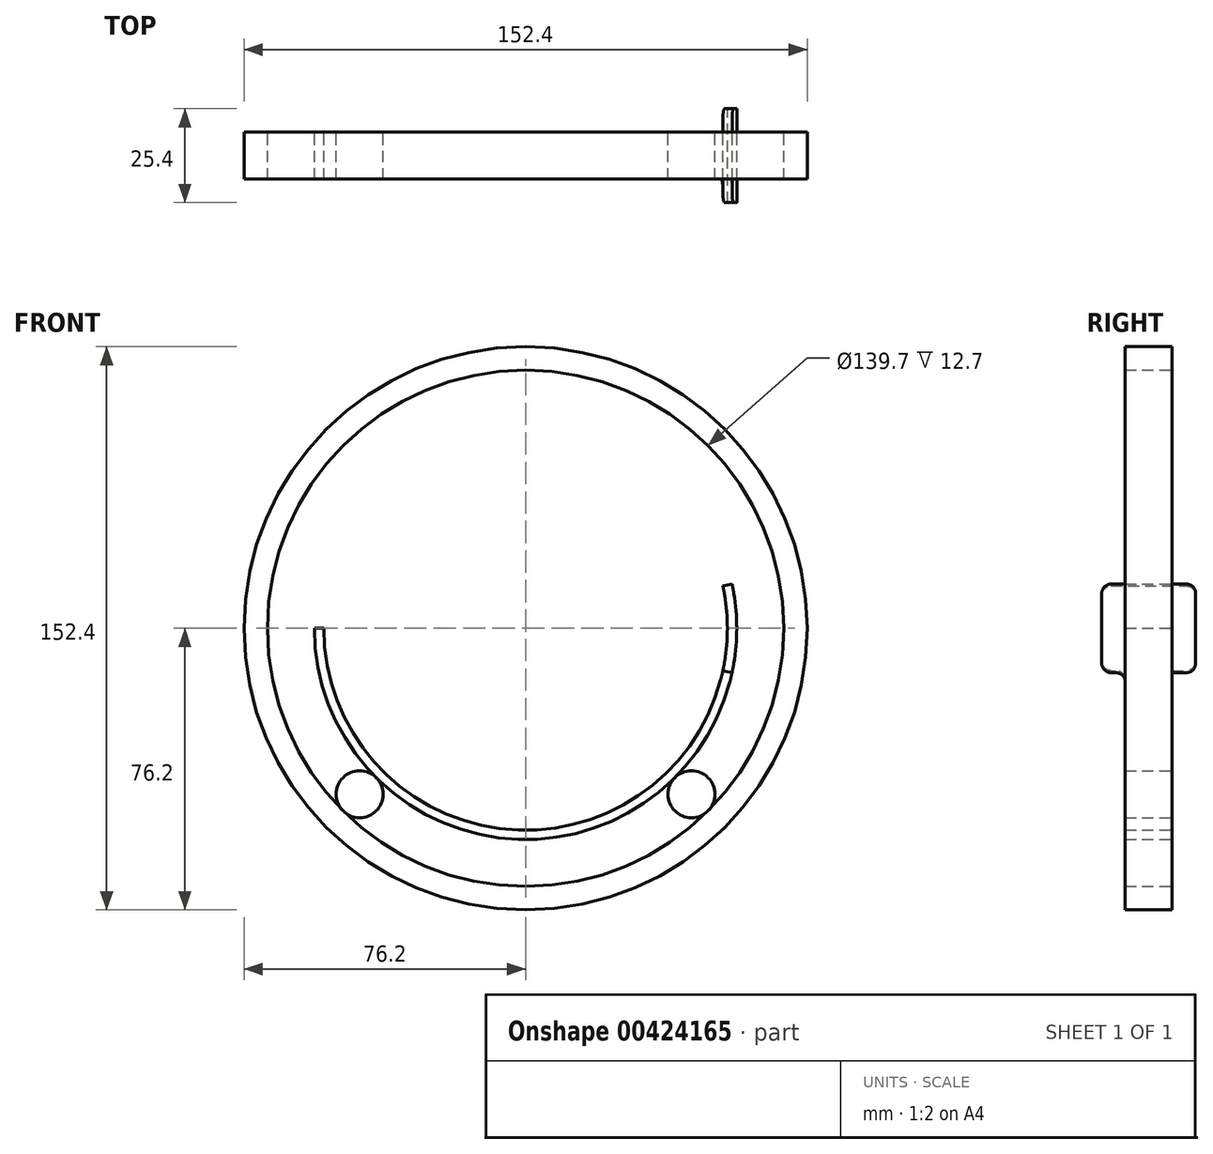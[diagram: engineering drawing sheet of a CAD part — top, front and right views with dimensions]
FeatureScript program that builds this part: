
annotation { "Feature Type Name" : "Feature", "Feature Type Description" : "" }
export const myFeature = defineFeature(function(context is Context, id is Id, definition is map)
    precondition{}
    {
        {
            assignVariable(context, id + "F0", {"name" : "SgAngle", "anyValue" : 45 * degree});
        }
        {
            var Q0;
            Q0=qCreatedBy(makeId("Front.planeOp"),FACE);
            var sketch = newSketch(context, id + "F1", { "sketchPlane" : qUnion([Q0])});
            skCircle(sketch, "E0", {"center": v(0, 0) * mm, "radius": 76.2 * mm});
            skCircle(sketch, "E1", {"center": v(0, 0) * mm, "radius": 69.85 * mm});
            skCircle(sketch, "E2", {"center": v(-44.9, -44.9) * mm, "radius": 6.35 * mm});
            skLineSegment(sketch, "E3", {"start": v(0, 0) * mm, "end": v(0, -76.2) * mm, "construction": true});
            skLineSegment(sketch, "E4", {"start": v(0, -76.2) * mm, "end": v(-76.2, -76.2) * mm, "construction": true});
            skLineSegment(sketch, "E5", {"start": v(-76.2, -76.2) * mm, "end": v(0, 0) * mm, "construction": true});
            skSolve(sketch);
        }
        {
            var Q0;
            Q0=makeQuery(id+"F1.imprint","IMPRINT",FACE,{"disambiguationData":[TD([[makeQuery(id+"F1.imprint","IMPRINT",EDGE,{"derivedFrom":sQuery(id+"F1.wireOp",EDGE,"E0")}),1.0]])]});
            var Q1;
            Q1=makeQuery(id+"F1.imprint","IMPRINT",FACE,{"disambiguationData":[TD([[makeQuery(id+"F1.imprint","IMPRINT",EDGE,{"derivedFrom":sQuery(id+"F1.wireOp",EDGE,"E2")}),1.0]])]});
            extrude(context, id + "F2", {"entities" : qUnion([Q0, Q1]), "endBound" : BoundingType.SYMMETRIC, "depth" : 12.7 * mm});
        }
        {
            var Q0;
            Q0=makeQuery(id+"F2.opExtrude","SWEPT_BODY",BODY,{"disambiguationData":[OSD([sQuery(id+"F1.wireOp",EDGE,"E2")])]});
            var Q1;
            Q1=makeQuery(id+"F2.opExtrude","CAP_EDGE",EDGE,{"disambiguationData":[OSD([sQuery(id+"F1.wireOp",EDGE,"E1")])],"isStart":false});
            circularPattern(context, id + "F3", {"entities" : qUnion([Q0]), "axis" : qUnion([Q1]), "angle" : getVariable(context, 'SgAngle') * 2, "instanceCount" : 2});
        }
        {
            var Q0;
            Q0=qCreatedBy(makeId("Front.planeOp"),FACE);
            var sketch = newSketch(context, id + "F4", { "sketchPlane" : qUnion([Q0])});
            skCircle(sketch, "E6", {"center": v(0, 0) * mm, "radius": 57.15 * mm});
            skCircle(sketch, "E7", {"center": v(0, 0) * mm, "radius": 54.61 * mm});
            skLineSegment(sketch, "E8", {"start": v(-85.74, 0) * mm, "end": v(91.38, 0) * mm});
            skLineSegment(sketch, "E9", {"start": v(0, 0) * mm, "end": v(78.53, 16.85) * mm});
            skLineSegment(sketch, "E10", {"start": v(0, 0) * mm, "end": v(79.08, -16.97) * mm});
            skSolve(sketch);
        }
        {
            var Q0;
            {var subQ0=sQuery(id+"F4.wireOp",EDGE,"E8");var subQ1=sQuery(id+"F4.wireOp",EDGE,"E6");var subQ2=makeQuery(id+"F4.imprint","INTERSECT",VERTEX,{"disambiguationData":[OD(1.0)],"derivedFrom":[subQ1,subQ0]});Q0=makeQuery(id+"F4.imprint","IMPRINT",FACE,{"disambiguationData":[TD([[makeQuery(id+"F4.imprint","IMPRINT",EDGE,{"disambiguationData":[TD([[subQ2,-1.0]])],"derivedFrom":subQ1}),1.0]])]});}
            extrude(context, id + "F5", {"entities" : qUnion([Q0]), "endBound" : BoundingType.SYMMETRIC, "depth" : 12.7 * mm});
        }
        {
            var Q0;
            {var subQ0=sQuery(id+"F4.wireOp",EDGE,"E9");var subQ1=sQuery(id+"F4.wireOp",EDGE,"E6");var subQ2=makeQuery(id+"F4.imprint","INTERSECT",VERTEX,{"derivedFrom":[subQ1,subQ0]});Q0=makeQuery(id+"F4.imprint","IMPRINT",FACE,{"disambiguationData":[TD([[makeQuery(id+"F4.imprint","IMPRINT",EDGE,{"disambiguationData":[TD([[subQ2,1.0]])],"derivedFrom":subQ1}),1.0]])]});}
            var Q1;
            {var subQ0=sQuery(id+"F4.wireOp",EDGE,"E8");var subQ1=sQuery(id+"F4.wireOp",EDGE,"E6");var subQ2=makeQuery(id+"F4.imprint","INTERSECT",VERTEX,{"disambiguationData":[OD(0.0)],"derivedFrom":[subQ1,subQ0]});Q1=makeQuery(id+"F4.imprint","IMPRINT",FACE,{"disambiguationData":[TD([[makeQuery(id+"F4.imprint","IMPRINT",EDGE,{"disambiguationData":[TD([[subQ2,1.0]])],"derivedFrom":subQ1}),1.0]])]});}
            extrude(context, id + "F6", {"entities" : qUnion([Q0, Q1]), "operationType" : NewBodyOperationType.ADD, "endBound" : BoundingType.SYMMETRIC, "depth" : 25.4 * mm});
        }
        {
            var Q0;
            Q0=makeQuery(id+"F5.opExtrude","CAP_EDGE",EDGE,{"disambiguationData":[OSD([sQuery(id+"F4.wireOp",EDGE,"E10")])],"isStart":true});
            var Q1;
            Q1=makeQuery(id+"F5.opExtrude","CAP_EDGE",EDGE,{"disambiguationData":[OSD([sQuery(id+"F4.wireOp",EDGE,"E10")])],"isStart":false});
            var Q2;
            Q2=makeQuery(id+"F6.opExtrude","CAP_EDGE",EDGE,{"disambiguationData":[OSD([sQuery(id+"F4.wireOp",EDGE,"E10")])],"isStart":false});
            var Q3;
            Q3=makeQuery(id+"F6.opExtrude","CAP_EDGE",EDGE,{"disambiguationData":[OSD([sQuery(id+"F4.wireOp",EDGE,"E10")])],"isStart":true});
            var Q4;
            Q4=makeQuery(id+"F6.opExtrude","CAP_EDGE",EDGE,{"disambiguationData":[OSD([sQuery(id+"F4.wireOp",EDGE,"E9")])],"isStart":false});
            var Q5;
            Q5=makeQuery(id+"F6.opExtrude","CAP_EDGE",EDGE,{"disambiguationData":[OSD([sQuery(id+"F4.wireOp",EDGE,"E9")])],"isStart":true});
            fillet(context, id + "F7", {"entities" : qUnion([Q0, Q1, Q2, Q3, Q4, Q5]), "radius" : 2.54 * mm, "tangentPropagation" : true, "allowEdgeOverflow" : false});
        }
    });
